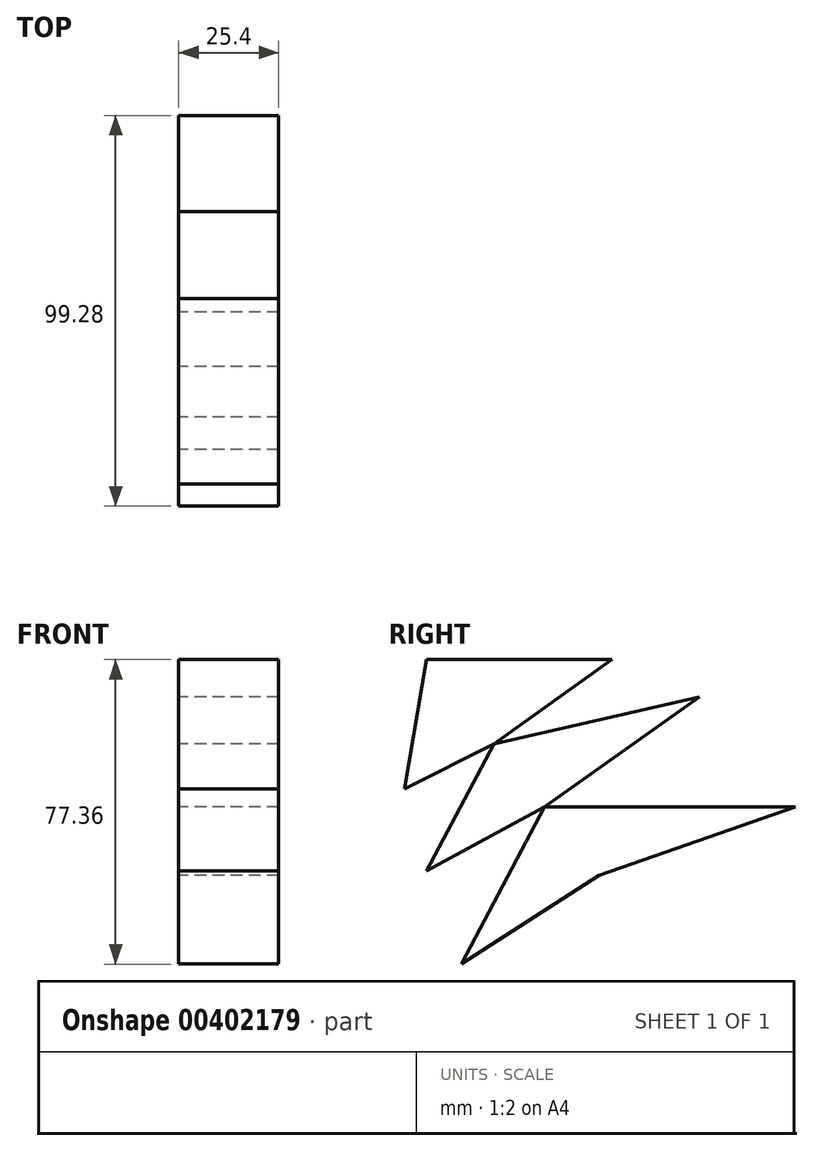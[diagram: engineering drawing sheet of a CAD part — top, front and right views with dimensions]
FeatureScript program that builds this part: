
annotation { "Feature Type Name" : "Feature", "Feature Type Description" : "" }
export const myFeature = defineFeature(function(context is Context, id is Id, definition is map)
    precondition{}
    {
        {
            var Q0;
            Q0=qCreatedBy(makeId("Right.planeOp"),FACE);
            var sketch = newSketch(context, id + "F0", { "sketchPlane" : qUnion([Q0])});
            skLineSegment(sketch, "E0", {"start": v(-65.65, 49.63) * mm, "end": v(-21.9, -5.23) * mm});
            skLineSegment(sketch, "E1", {"start": v(-65.65, 49.63) * mm, "end": v(-18.54, 49.63) * mm});
            skLineSegment(sketch, "E2", {"start": v(-18.54, 49.63) * mm, "end": v(-48.6, 28.24) * mm});
            skLineSegment(sketch, "E3", {"start": v(-48.6, 28.24) * mm, "end": v(3.62, 40.18) * mm});
            skLineSegment(sketch, "E4", {"start": v(3.62, 40.18) * mm, "end": v(-35.76, 12.15) * mm});
            skLineSegment(sketch, "E5", {"start": v(-35.76, 12.15) * mm, "end": v(28.05, 12.15) * mm});
            skLineSegment(sketch, "E6", {"start": v(28.05, 12.15) * mm, "end": v(-21.9, -5.23) * mm});
            skLineSegment(sketch, "E7", {"start": v(-65.65, 49.63) * mm, "end": v(-71.23, 16.74) * mm});
            skLineSegment(sketch, "E8", {"start": v(-71.23, 16.74) * mm, "end": v(-48.6, 28.24) * mm});
            skLineSegment(sketch, "E9", {"start": v(-48.6, 28.24) * mm, "end": v(-65.65, -4.05) * mm});
            skLineSegment(sketch, "E10", {"start": v(-65.65, -4.05) * mm, "end": v(-35.76, 12.15) * mm});
            skLineSegment(sketch, "E11", {"start": v(-35.76, 12.15) * mm, "end": v(-56.83, -27.73) * mm});
            skLineSegment(sketch, "E12", {"start": v(-56.83, -27.73) * mm, "end": v(-21.9, -5.23) * mm});
            skSolve(sketch);
        }
        {
            var Q0;
            Q0 = qSketchRegion(id + "F0", true);
            extrude(context, id + "F1", {"entities" : qUnion([Q0]), "depth" : 25.4 * mm});
        }
        {
            var Q0;
            Q0 = qSketchRegion(id + "F0", true);
            extrude(context, id + "F2", {"entities" : qUnion([Q0]), "depth" : 25.4 * mm});
        }
    });
